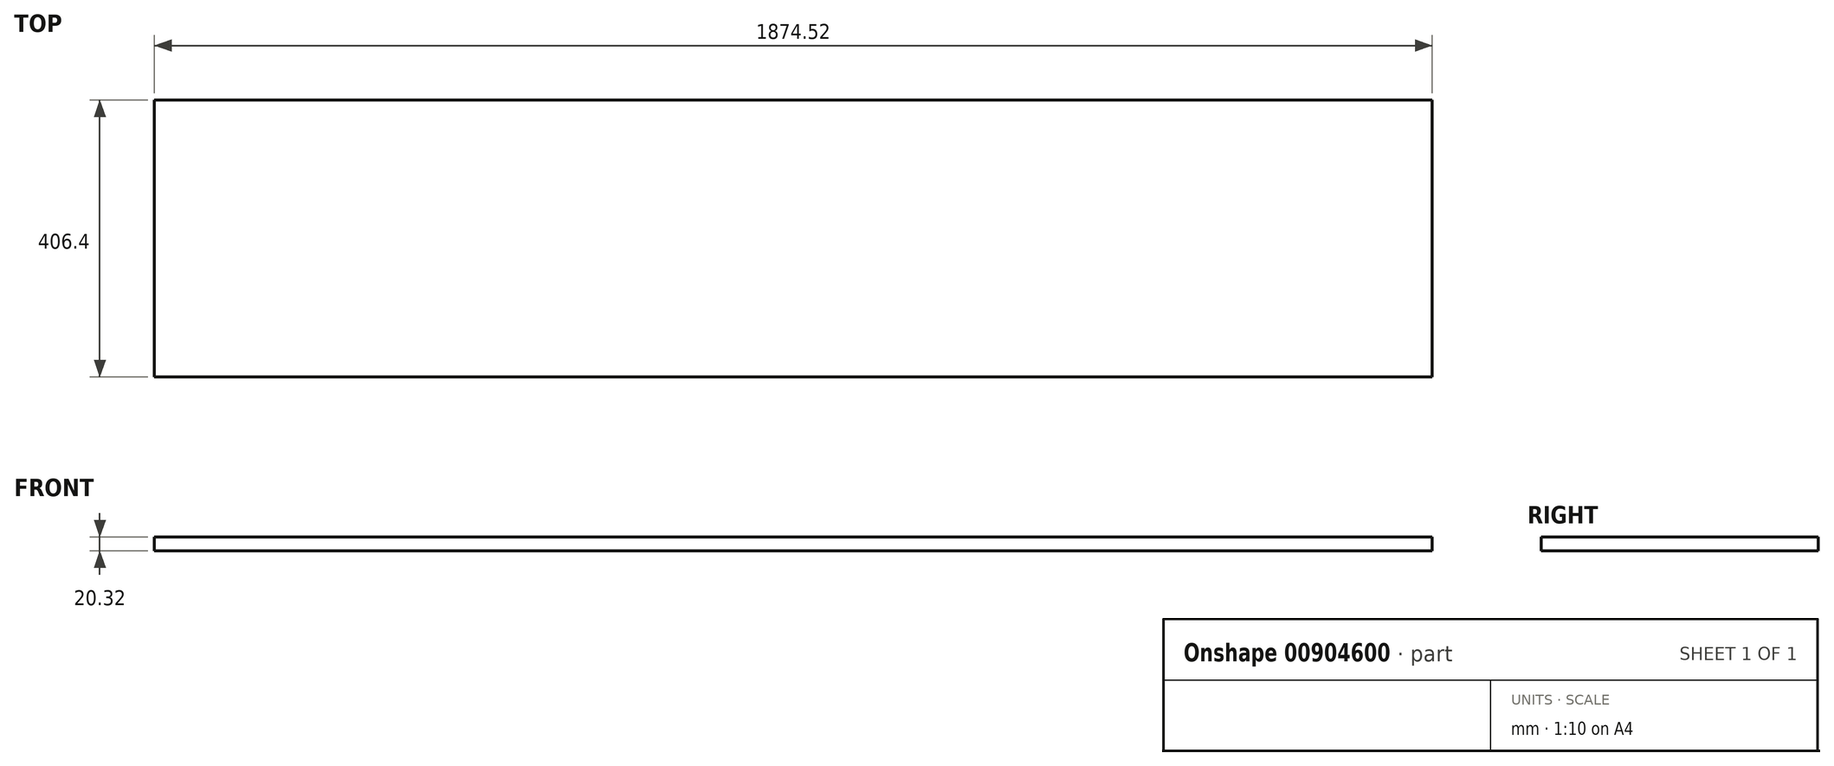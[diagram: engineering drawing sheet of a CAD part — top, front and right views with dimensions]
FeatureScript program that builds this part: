
annotation { "Feature Type Name" : "Feature", "Feature Type Description" : "" }
export const myFeature = defineFeature(function(context is Context, id is Id, definition is map)
    precondition{}
    {
        {
            var Q0;
            Q0=qCreatedBy(makeId("Top.planeOp"),FACE);
            var sketch = newSketch(context, id + "F0", { "sketchPlane" : qUnion([Q0])});
            skLineSegment(sketch, "E0.bottom", {"start": v(937.26, -203.2) * mm, "end": v(-937.26, -203.2) * mm});
            skLineSegment(sketch, "E0.top", {"start": v(937.26, 203.2) * mm, "end": v(-937.26, 203.2) * mm});
            skLineSegment(sketch, "E0.left", {"start": v(937.26, -203.2) * mm, "end": v(937.26, 203.2) * mm});
            skLineSegment(sketch, "E0.right", {"start": v(-937.26, -203.2) * mm, "end": v(-937.26, 203.2) * mm});
            skPoint(sketch, "E0.middle", {"position": v(0, 0) * mm});
            skPoint(sketch, "E1", {"position": v(-937.26, -152.4) * mm});
            skPoint(sketch, "E2", {"position": v(-937.26, 152.4) * mm});
            skSolve(sketch);
        }
        {
            var Q0;
            Q0=makeQuery(id+"F0.imprint","IMPRINT",FACE,{"disambiguationData":[TD([[makeQuery(id+"F0.imprint","IMPRINT",EDGE,{"derivedFrom":sQuery(id+"F0.wireOp",EDGE,"E0.bottom")}),-1.0]])]});
            extrude(context, id + "F1", {"entities" : qUnion([Q0]), "depth" : 20.32 * mm, "offsetDistance" : 25.4 * mm});
        }
    });
